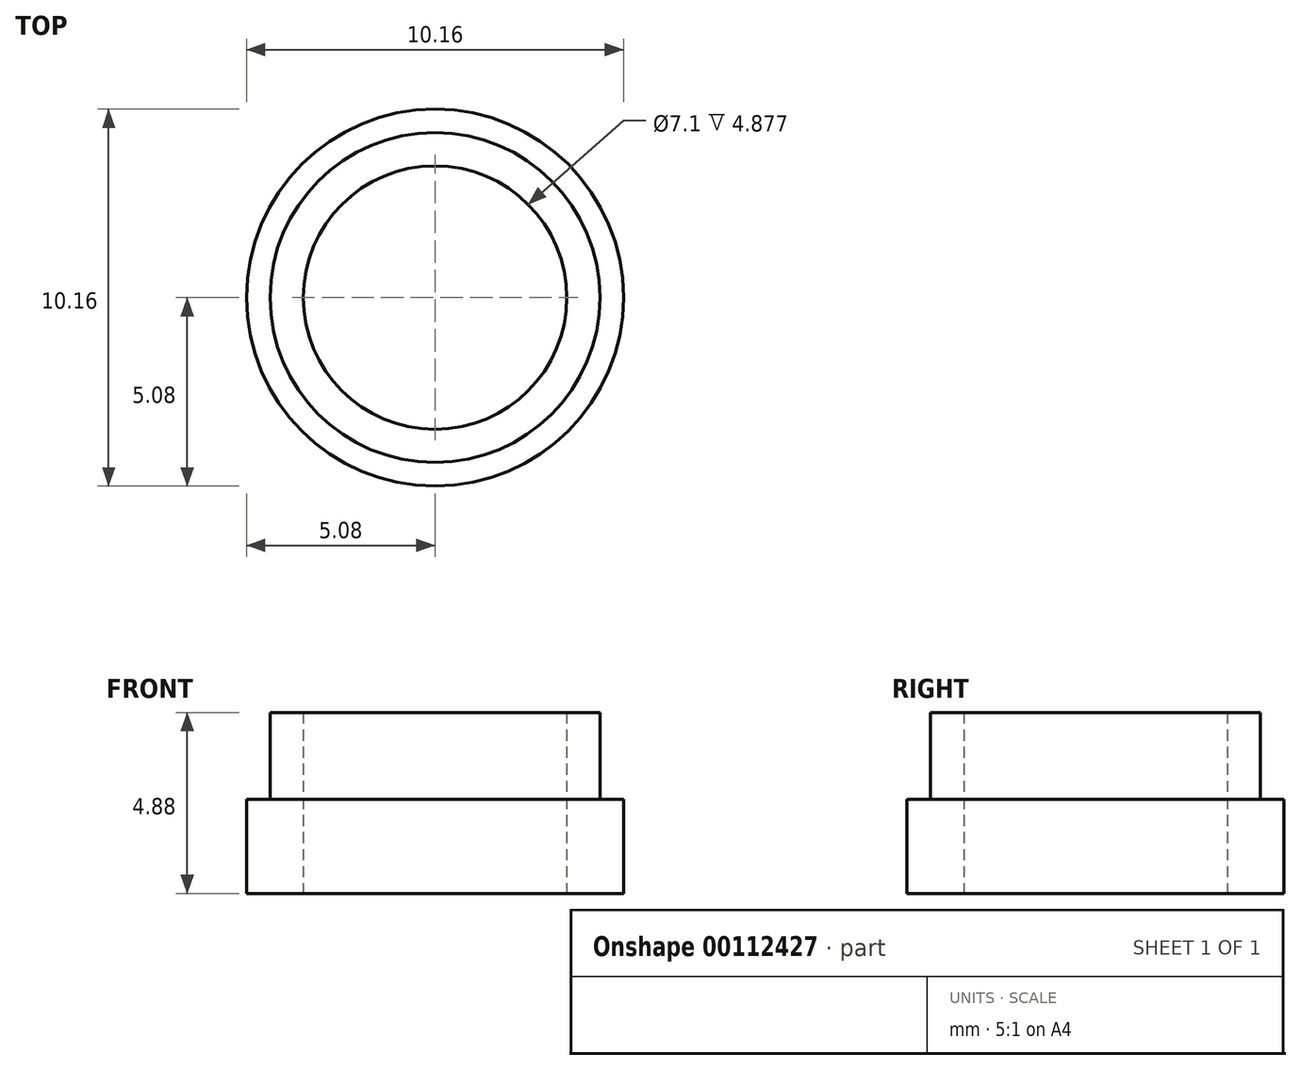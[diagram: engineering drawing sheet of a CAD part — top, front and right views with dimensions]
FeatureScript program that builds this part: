
annotation { "Feature Type Name" : "Feature", "Feature Type Description" : "" }
export const myFeature = defineFeature(function(context is Context, id is Id, definition is map)
    precondition{}
    {
        {
            var Q0;
            Q0=qCreatedBy(makeId("Top.planeOp"),FACE);
            var sketch = newSketch(context, id + "F0", { "sketchPlane" : qUnion([Q0])});
            skCircle(sketch, "E0", {"center": v(0, 0) * mm, "radius": 5.08 * mm});
            skCircle(sketch, "E1", {"center": v(0, 0) * mm, "radius": 3.55 * mm});
            skSolve(sketch);
        }
        {
            var Q0;
            Q0 = qSketchRegion(id + "F0", true);
            extrude(context, id + "F1", {"entities" : qUnion([Q0]), "depth" : 2.54 * mm, "offsetDistance" : 25 * mm});
        }
        {
            var Q0;
            Q0=makeQuery(id+"F1.opExtrude","CAP_FACE",FACE,{"disambiguationData":[OSD([sQuery(id+"F0.wireOp",EDGE,"E0"),sQuery(id+"F0.wireOp",EDGE,"E1")])],"isStart":false});
            var sketch = newSketch(context, id + "F2", { "sketchPlane" : qUnion([Q0])});
            skCircle(sketch, "E2", {"center": v(0, 0) * mm, "radius": 3.55 * mm});
            skCircle(sketch, "E3", {"center": v(0, 0) * mm, "radius": 4.45 * mm});
            skSolve(sketch);
        }
        {
            var Q0;
            Q0 = qSketchRegion(id + "F2", true);
            extrude(context, id + "F3", {"entities" : qUnion([Q0]), "operationType" : NewBodyOperationType.ADD, "depth" : 2.34 * mm, "offsetDistance" : 25 * mm});
        }
    });
